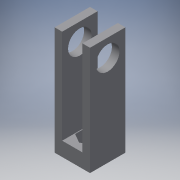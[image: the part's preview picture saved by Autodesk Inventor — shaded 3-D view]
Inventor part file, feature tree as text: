
AUTODESK INVENTOR PART (.ipt)
format: ipt  version: 2016 (Build 200138000, 138)  size: 144,384 bytes
history: native  units: in
note: dims shown in document units (in); Inventor stores cm internally (conversion verified against a paired STEP export)
features: extrude x5, sketch x5
ambient origin geometry x8: Origin, YZ Plane, XZ Plane, XY Plane, X Axis, Y Axis, Z Axis, Center Point
bodies: Solid1 (feature_tree)
feature tree (10):
  extrude  "Extrusion1"  Depth=0.75in
  extrude  "Extrusion2"  Depth=0.4in
  extrude  "Extrusion3"  Depth=0.375in
  extrude  "Extrusion4"  Depth=0.25in
  extrude  "Extrusion5"  Depth=0.75in
  sketch  "Sketch1"  dims[d0=0.75in d1=0.75in]
  sketch  "Sketch2"  dims[d2=0.3in d3=0.0in d4=0.4in]
  sketch  "Sketch3"  dims[d5=0.375in d6=0.375in]
  sketch  "Sketch4"  dims[d7=0.25in d8=0.0in d9=0.19in]
  sketch  "Sketch5"  dims[d10=0.2in d11=0.2in d12=0.5in d13=0.0in d14=0.16in d15=0.16in d16=2.0in d17=0.0in d18=0.5in d19=0.375in d20=0.375in d21=0.75in d22=0.0in]
